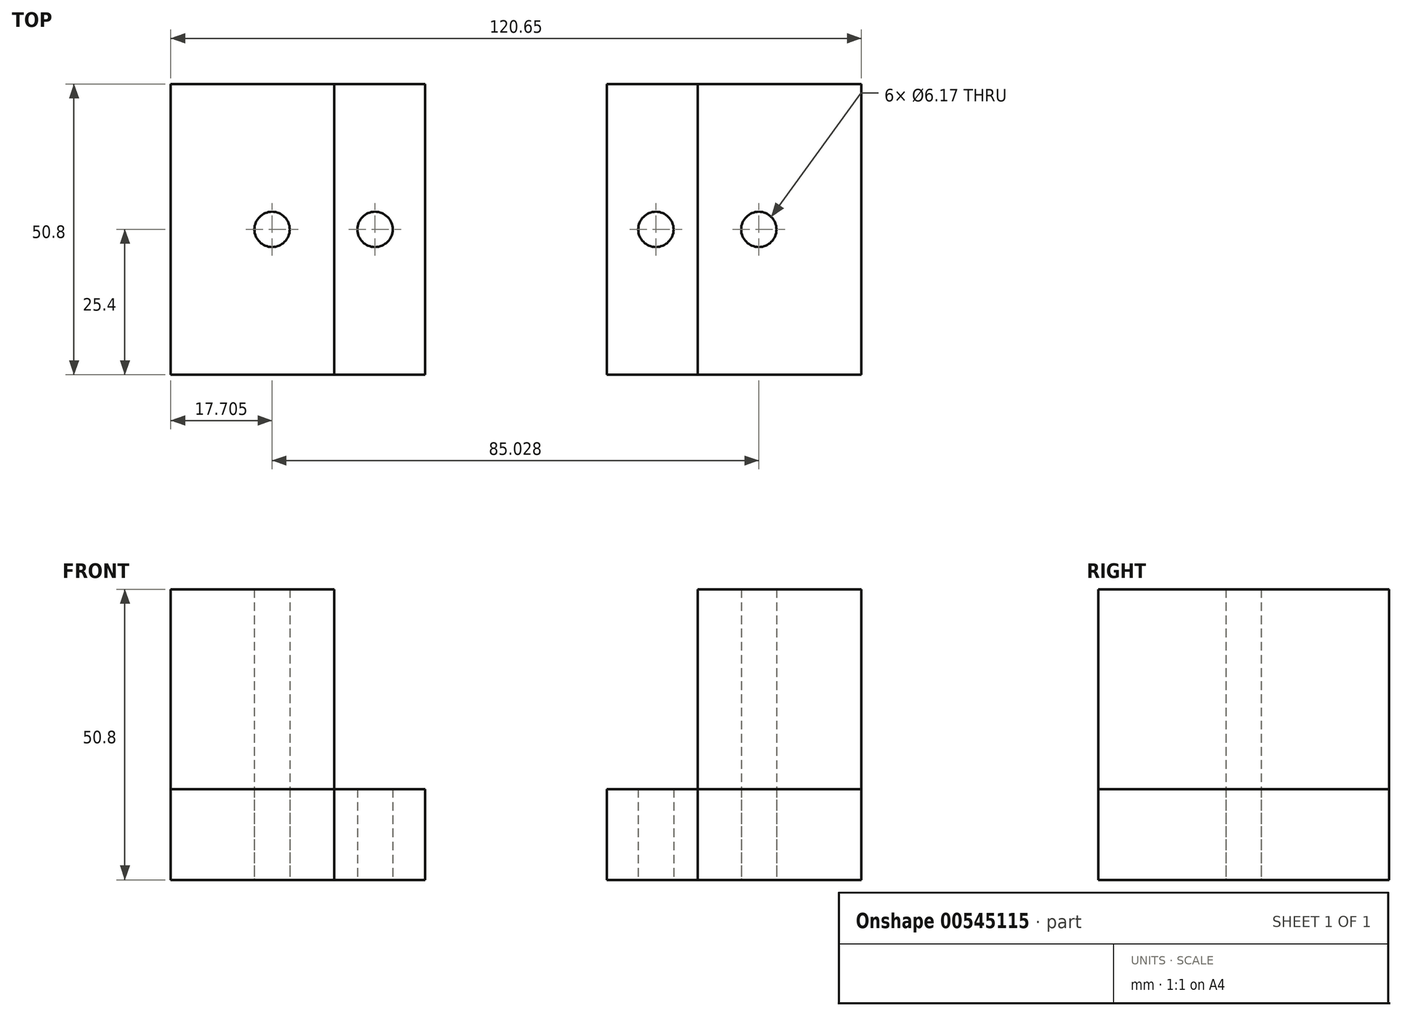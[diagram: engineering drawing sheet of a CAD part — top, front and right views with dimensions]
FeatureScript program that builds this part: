
annotation { "Feature Type Name" : "Feature", "Feature Type Description" : "" }
export const myFeature = defineFeature(function(context is Context, id is Id, definition is map)
    precondition{}
    {
        {
            var Q0;
            Q0=qCreatedBy(makeId("Top.planeOp"),FACE);
            var sketch = newSketch(context, id + "F0", { "sketchPlane" : qUnion([Q0])});
            skLineSegment(sketch, "E0", {"start": v(-49.06, 0) * mm, "end": v(0.21, 0) * mm});
            skCircle(sketch, "E1", {"center": v(-49.06, 0) * mm, "radius": 3.09 * mm});
            skCircle(sketch, "E2", {"center": v(0, 0) * mm, "radius": 3.09 * mm});
            skCircle(sketch, "E3.1.0.0", {"center": v(-67.05, 0) * mm, "radius": 3.09 * mm});
            skLineSegment(sketch, "E3.direction1", {"start": v(-49.06, 0) * mm, "end": v(-67.05, 0) * mm, "construction": true});
            skCircle(sketch, "E4.1.0.0", {"center": v(17.98, 0) * mm, "radius": 3.09 * mm});
            skLineSegment(sketch, "E4.direction1", {"start": v(0, 0) * mm, "end": v(17.98, 0) * mm, "construction": true});
            skLineSegment(sketch, "E5", {"start": v(7.33, 25.4) * mm, "end": v(7.33, -25.4) * mm});
            skLineSegment(sketch, "E6", {"start": v(-56.17, 25.4) * mm, "end": v(-56.17, -25.4) * mm});
            skLineSegment(sketch, "E7", {"start": v(-8.55, 25.4) * mm, "end": v(-8.55, -25.4) * mm});
            skLineSegment(sketch, "E8", {"start": v(-40.3, 25.4) * mm, "end": v(-40.3, -25.4) * mm});
            skLineSegment(sketch, "E9", {"start": v(35.9, 25.4) * mm, "end": v(35.9, -25.4) * mm});
            skLineSegment(sketch, "E10", {"start": v(-84.75, 25.4) * mm, "end": v(-84.75, -25.4) * mm});
            skLineSegment(sketch, "E11", {"start": v(-84.75, 25.4) * mm, "end": v(-40.3, 25.4) * mm});
            skLineSegment(sketch, "E12", {"start": v(35.9, -25.4) * mm, "end": v(-8.55, -25.4) * mm});
            skLineSegment(sketch, "E13.trimOffspring", {"start": v(-40.3, -25.4) * mm, "end": v(-84.75, -25.4) * mm});
            skLineSegment(sketch, "E14.trimOffspring", {"start": v(-8.55, 25.4) * mm, "end": v(35.9, 25.4) * mm});
            skPoint(sketch, "E15.start.orphan", {"position": v(-24.42, 0) * mm});
            skSolve(sketch);
        }
        {
            var Q0;
            Q0=makeQuery(id+"F0.imprint","IMPRINT",FACE,{"disambiguationData":[TD([[makeQuery(id+"F0.imprint","IMPRINT",EDGE,{"derivedFrom":sQuery(id+"F0.wireOp",EDGE,"E3.1.0.0")}),-1.0]])]});
            var Q1;
            Q1=makeQuery(id+"F0.imprint","IMPRINT",FACE,{"disambiguationData":[TD([[makeQuery(id+"F0.imprint","IMPRINT",EDGE,{"derivedFrom":sQuery(id+"F0.wireOp",EDGE,"E4.1.0.0")}),-1.0]])]});
            extrude(context, id + "F1", {"entities" : qUnion([Q0, Q1]), "depth" : 50.8 * mm, "offsetDistance" : 25.4 * mm});
        }
        {
            var Q0;
            Q0 = qSketchRegion(id + "F0", true);
            extrude(context, id + "F2", {"entities" : qUnion([Q0]), "depth" : 15.88 * mm, "offsetDistance" : 25.4 * mm});
        }
    });
